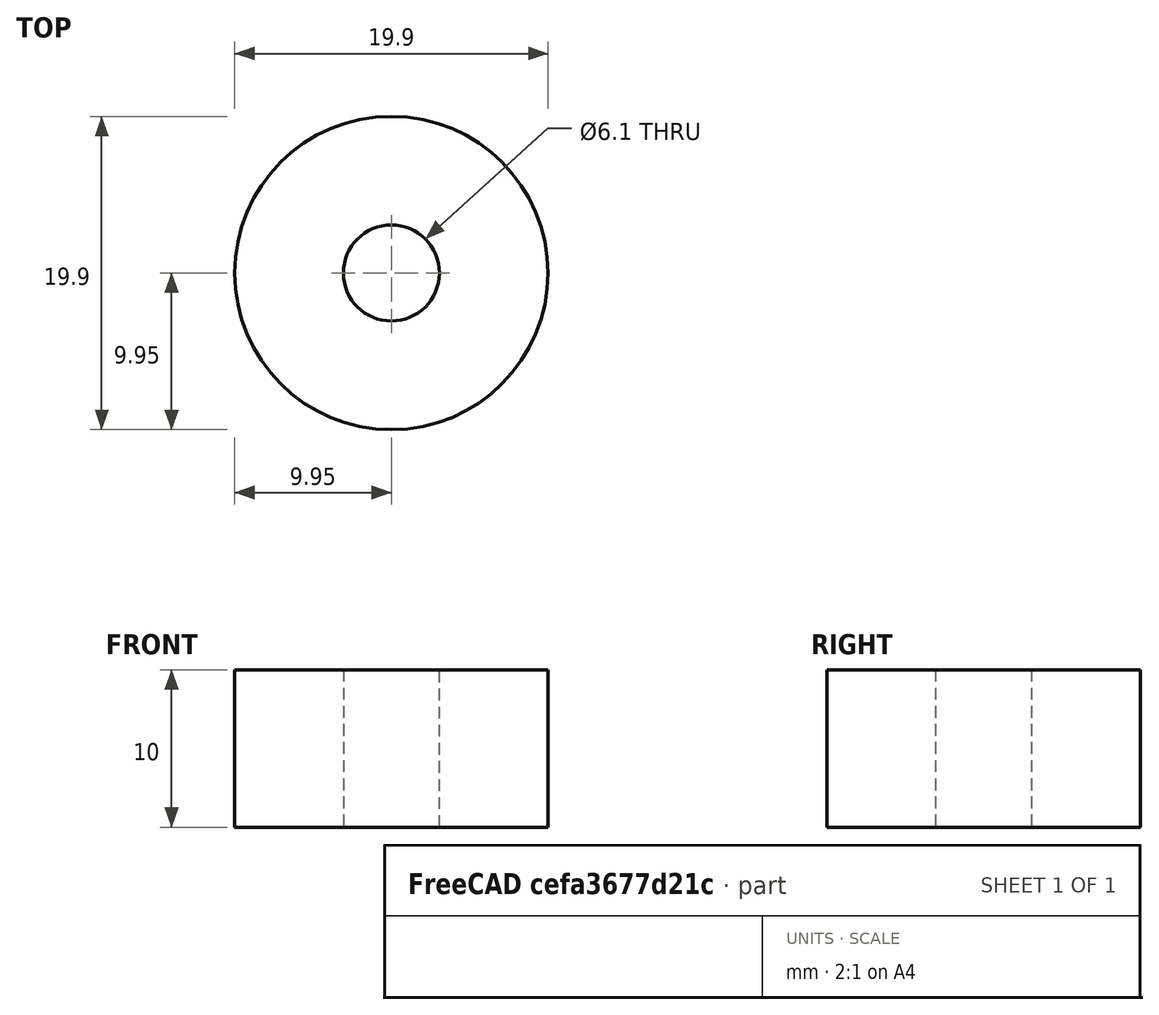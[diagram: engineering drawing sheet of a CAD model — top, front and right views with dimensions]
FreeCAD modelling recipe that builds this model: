
FCSTD DOCUMENT  (FreeCAD 0.20R27319 (Git))
Label: TestStop
License: All rights reserved
LicenseURL: http://en.wikipedia.org/wiki/All_rights_reserved
objects: Sketcher::SketchObject×1, PartDesign::Pad×1, PartDesign::Body×1
note: 4 computed .brp shape members not serialized (recipe doc carries the construction recipe); baked Part::Feature solids carry a one-line shape summary decoded from their .brp
EXTERNAL_REF file=SharedDimensions.FCStd obj=Spreadsheet

FEATURE [Sketcher::SketchObject] Sketch001
  FullyConstrained = true
  MapMode = 5
  Placement = pos=(0,0,8) rot=(0,0,1;0rad)
  expr: Constraints[1] = SharedDimensions#Spreadsheet.HoleDiameter - SharedDimensions#Spreadsheet.HoleClearance
  expr: Constraints[3] = SharedDimensions#Spreadsheet.BoltDiameter
  sketch-geometry (2):
    g0: Circle CenterX=0 CenterY=0 CenterZ=0 NormalX=0 NormalY=0 NormalZ=1 AngleXU=0 Radius=9.95
    g1: Circle CenterX=0 CenterY=0 CenterZ=0 NormalX=0 NormalY=0 NormalZ=1 AngleXU=0 Radius=3.05
  constraints (4):
    c: Coincident(g0,g-1)
    c: Diameter(g0) = 19.9
    c: Coincident(g1,g0)
    c: Diameter(g1) = 6.1
FEATURE [PartDesign::Pad] Pad
  Direction = (0,0,1)
  Length = 10
  Length2 = 10
  Placement = pos=(0,0,8) rot=(0,0,1;0rad)
  Profile = -> Sketch001
  ReferenceAxis = -> Sketch001 [N_Axis]
  Type = 0
FEATURE [PartDesign::Body] Body
  Group = -> [Sketch001,Pad]
  Origin = -> Origin
  Tip = -> Pad
